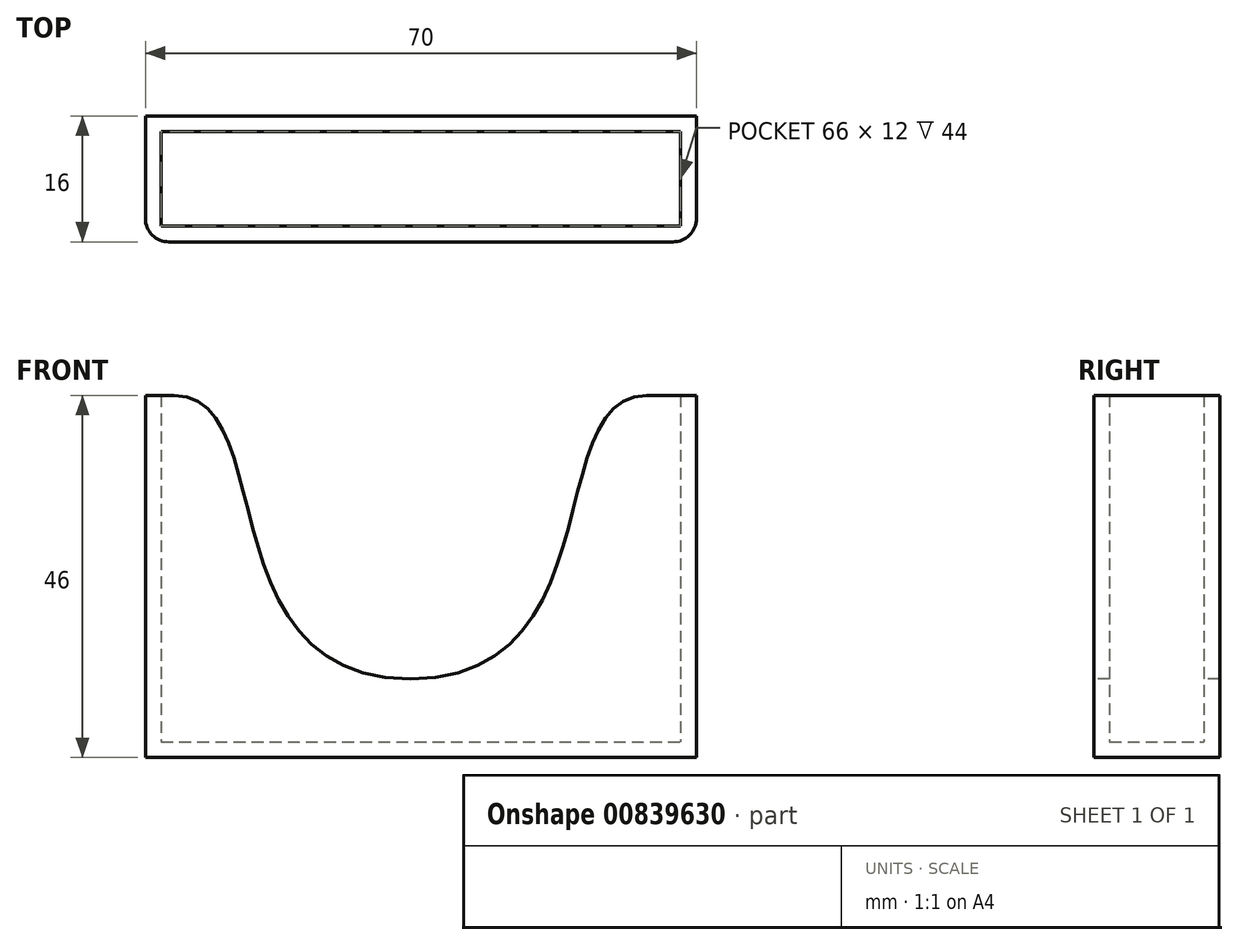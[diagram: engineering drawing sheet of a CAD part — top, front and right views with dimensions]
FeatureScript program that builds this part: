
annotation { "Feature Type Name" : "Feature", "Feature Type Description" : "" }
export const myFeature = defineFeature(function(context is Context, id is Id, definition is map)
    precondition{}
    {
        {
            var Q0;
            Q0=qCreatedBy(makeId("Top.planeOp"),FACE);
            var sketch = newSketch(context, id + "F0", { "sketchPlane" : qUnion([Q0])});
            skLineSegment(sketch, "E0.bottom", {"start": v(-33.68, -8) * mm, "end": v(36.32, -8) * mm});
            skLineSegment(sketch, "E0.top", {"start": v(-33.68, 8) * mm, "end": v(36.32, 8) * mm});
            skLineSegment(sketch, "E0.left", {"start": v(-33.68, -8) * mm, "end": v(-33.68, 8) * mm});
            skLineSegment(sketch, "E0.right", {"start": v(36.32, -8) * mm, "end": v(36.32, 8) * mm});
            skSolve(sketch);
        }
        {
            var Q0;
            Q0=makeQuery(id+"F0.imprint","IMPRINT",FACE,{"disambiguationData":[TD([[makeQuery(id+"F0.imprint","IMPRINT",EDGE,{"derivedFrom":sQuery(id+"F0.wireOp",EDGE,"E0.bottom")}),1.0]])]});
            extrude(context, id + "F1", {"entities" : qUnion([Q0]), "depth" : 46 * mm, "offsetDistance" : 25 * mm});
        }
        {
            var Q0;
            Q0=makeQuery(id+"F1.opExtrude","CAP_FACE",FACE,{"disambiguationData":[OSD([sQuery(id+"F0.wireOp",EDGE,"E0.bottom"),sQuery(id+"F0.wireOp",EDGE,"E0.top"),sQuery(id+"F0.wireOp",EDGE,"E0.left"),sQuery(id+"F0.wireOp",EDGE,"E0.right")])],"isStart":false});
            shell(context, id + "F2", {"entities" : qUnion([Q0]), "thickness" : 2 * mm});
        }
        {
            var Q0;
            Q0=makeQuery(id+"F1.opExtrude","SWEPT_FACE",FACE,{"disambiguationData":[OSD([sQuery(id+"F0.wireOp",EDGE,"E0.bottom")])]});
            var sketch = newSketch(context, id + "F3", { "sketchPlane" : qUnion([Q0])});
            skLineSegment(sketch, "E1", {"start": v(-30, 46) * mm, "end": v(0, 46) * mm});
            skFitSpline(sketch, "E2", {"points": [v(-30, 46) * mm, v(0, 10) * mm], "startDerivative": vector(40.48, 0) * mm, "endDerivative": vector(78.28, 0) * mm});
            skLineSegment(sketch, "E3.MirrorCS", {"start": v(30, 46) * mm, "end": v(0, 46) * mm});
            skFitSpline(sketch, "E4.MirrorCS", {"points": [v(30, 46) * mm, v(0, 10) * mm], "startDerivative": vector(-40.48, 0) * mm, "endDerivative": vector(-78.28, 0) * mm});
            skSolve(sketch);
        }
        {
            var Q0;
            Q0=makeQuery(id+"F3.imprint","IMPRINT",FACE,{"disambiguationData":[TD([[makeQuery(id+"F3.imprint","IMPRINT",EDGE,{"derivedFrom":sQuery(id+"F3.wireOp",EDGE,"E1")}),-1.0]])]});
            extrude(context, id + "F4", {"entities" : qUnion([Q0]), "operationType" : NewBodyOperationType.REMOVE, "oppositeDirection" : true, "depth" : 100 * mm, "offsetDistance" : 25 * mm});
        }
        {
            var Q0;
            Q0=makeQuery(id+"F1.opExtrude","SWEPT_EDGE",EDGE,{"disambiguationData":[OSD([sQuery(id+"F0.wireOp",EDGE,"E0.bottom"),sQuery(id+"F0.wireOp",EDGE,"E0.left")])]});
            var Q1;
            Q1=makeQuery(id+"F1.opExtrude","SWEPT_EDGE",EDGE,{"disambiguationData":[OSD([sQuery(id+"F0.wireOp",EDGE,"E0.bottom"),sQuery(id+"F0.wireOp",EDGE,"E0.right")])]});
            fillet(context, id + "F5", {"entities" : qUnion([Q0, Q1]), "radius" : 3 * mm, "tangentPropagation" : true, "allowEdgeOverflow" : false});
        }
    });
